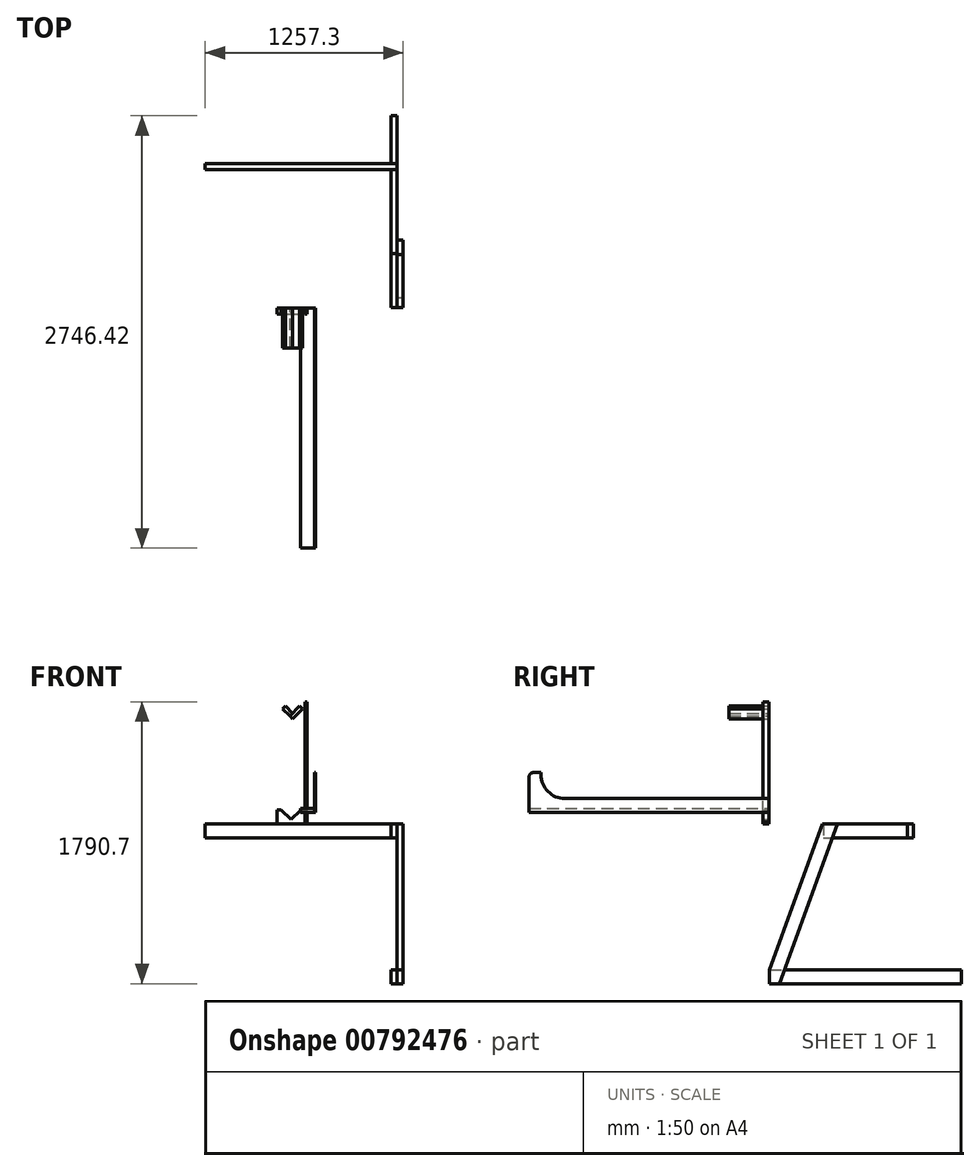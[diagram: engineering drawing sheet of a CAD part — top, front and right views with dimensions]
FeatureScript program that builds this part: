
annotation { "Feature Type Name" : "Feature", "Feature Type Description" : "" }
export const myFeature = defineFeature(function(context is Context, id is Id, definition is map)
    precondition{}
    {
        {
            var Q0;
            Q0=qCreatedBy(makeId("Right.planeOp"),FACE);
            var sketch = newSketch(context, id + "F0", { "sketchPlane" : qUnion([Q0])});
            skCircle(sketch, "E0", {"center": v(0, 368.3) * mm, "radius": 368.3 * mm, "construction": true});
            skLineSegment(sketch, "E1", {"start": v(0, 0) * mm, "end": v(2298.17, 0) * mm, "construction": true});
            skLineSegment(sketch, "E2", {"start": v(-368.3, 745.94) * mm, "end": v(-368.3, 0) * mm, "construction": true});
            skCircle(sketch, "E3", {"center": v(1157.3, 368.3) * mm, "radius": 368.3 * mm, "construction": true});
            skLineSegment(sketch, "E4", {"start": v(281.32, 941.93) * mm, "end": v(431.44, 558.5) * mm, "construction": true});
            skLineSegment(sketch, "E5", {"start": v(348.24, 558.5) * mm, "end": v(0, 368.3) * mm, "construction": true});
            skLineSegment(sketch, "E6", {"start": v(0, 368.3) * mm, "end": v(431.44, 343.27) * mm, "construction": true});
            skLineSegment(sketch, "E7", {"start": v(431.44, 343.27) * mm, "end": v(567.09, 368.3) * mm, "construction": true});
            skLineSegment(sketch, "E8", {"start": v(567.09, 368.3) * mm, "end": v(811.25, 847.88) * mm, "construction": true});
            skLineSegment(sketch, "E9", {"start": v(811.25, 847.88) * mm, "end": v(912.54, 907.57) * mm, "construction": true});
            skLineSegment(sketch, "E10", {"start": v(867.32, 967.25) * mm, "end": v(1120.53, 368.3) * mm, "construction": true});
            skLineSegment(sketch, "E11", {"start": v(867.32, 967.25) * mm, "end": v(409.73, 650.74) * mm, "construction": true});
            skLineSegment(sketch, "E12", {"start": v(346.7, 774.93) * mm, "end": v(556.87, 752.52) * mm, "construction": true});
            skLineSegment(sketch, "E13", {"start": v(125.78, 1032.36) * mm, "end": v(384.41, 1032.36) * mm, "construction": true});
            skCircle(sketch, "E14", {"center": v(1157.3, 368.3) * mm, "radius": 101.6 * mm, "construction": true});
            skCircle(sketch, "E15", {"center": v(0, 368.3) * mm, "radius": 88.9 * mm, "construction": true});
            skSolve(sketch);
        }
        {
            var Q0;
            Q0=qCreatedBy(makeId("Right.planeOp"),FACE);
            var sketch = newSketch(context, id + "F1", { "sketchPlane" : qUnion([Q0])});
            skCircle(sketch, "E16", {"center": v(0, 1519.87) * mm, "radius": 368.3 * mm});
            skCircle(sketch, "E17", {"center": v(1155.64, 1531.5) * mm, "radius": 368.3 * mm});
            skLineSegment(sketch, "E18", {"start": v(0, 1519.87) * mm, "end": v(1155.64, 1531.5) * mm});
            skLineSegment(sketch, "E19", {"start": v(120.35, 2245.02) * mm, "end": v(884.9, 2252.7) * mm});
            skLineSegment(sketch, "E20", {"start": v(0, 1519.87) * mm, "end": v(120.35, 2245.02) * mm});
            skLineSegment(sketch, "E21", {"start": v(884.9, 2252.7) * mm, "end": v(1155.64, 1531.5) * mm});
            skSolve(sketch);
        }
        {
            var Q0;
            Q0=qCreatedBy(makeId("Right.planeOp"),FACE);
            var sketch = newSketch(context, id + "F2", { "sketchPlane" : qUnion([Q0])});
            skLineSegment(sketch, "E22.bottom", {"start": v(3.22, 177.8) * mm, "end": v(1222.42, 177.8) * mm});
            skLineSegment(sketch, "E22.top", {"start": v(3.22, 88.9) * mm, "end": v(1222.42, 88.9) * mm});
            skLineSegment(sketch, "E22.left", {"start": v(3.22, 177.8) * mm, "end": v(3.22, 88.9) * mm});
            skLineSegment(sketch, "E22.right", {"start": v(1222.42, 177.8) * mm, "end": v(1222.42, 88.9) * mm});
            skLineSegment(sketch, "E23.bottom", {"start": v(308.02, 1104.9) * mm, "end": v(917.62, 1104.9) * mm});
            skLineSegment(sketch, "E23.top", {"start": v(308.02, 1016) * mm, "end": v(917.62, 1016) * mm});
            skLineSegment(sketch, "E23.left", {"start": v(308.02, 1104.9) * mm, "end": v(308.02, 1016) * mm});
            skLineSegment(sketch, "E23.right", {"start": v(917.62, 1104.9) * mm, "end": v(917.62, 1016) * mm});
            skLineSegment(sketch, "E24", {"start": v(308.02, 1016) * mm, "end": v(3.22, 177.8) * mm});
            skLineSegment(sketch, "E25", {"start": v(917.62, 1016) * mm, "end": v(1222.42, 177.8) * mm});
            skLineSegment(sketch, "E26", {"start": v(823.02, 1016) * mm, "end": v(1127.82, 177.8) * mm});
            skLineSegment(sketch, "E27", {"start": v(434.94, 1104.9) * mm, "end": v(65.49, 88.9) * mm});
            skPoint(sketch, "E28", {"position": v(612.82, 1016) * mm});
            skPoint(sketch, "E29", {"position": v(612.82, 177.8) * mm});
            skPoint(sketch, "E30", {"position": v(612.82, 1104.9) * mm});
            skLineSegment(sketch, "E31", {"start": v(879.52, 1104.9) * mm, "end": v(879.52, 1016) * mm});
            skLineSegment(sketch, "E32", {"start": v(346.12, 1104.9) * mm, "end": v(346.12, 1016) * mm});
            skLineSegment(sketch, "E33", {"start": v(3.22, 177.8) * mm, "end": v(308.02, 1104.9) * mm, "construction": true});
            skSolve(sketch);
        }
        {
            var Q0;
            Q0=qCreatedBy(makeId("Right.planeOp"),FACE);
            var sketch = newSketch(context, id + "F3", { "sketchPlane" : qUnion([Q0])});
            skLineSegment(sketch, "E34.bottom", {"start": v(346.12, 1104.9) * mm, "end": v(879.52, 1104.9) * mm});
            skLineSegment(sketch, "E34.top", {"start": v(346.12, 1016) * mm, "end": v(879.52, 1016) * mm});
            skLineSegment(sketch, "E34.left", {"start": v(346.12, 1104.9) * mm, "end": v(346.12, 1016) * mm});
            skLineSegment(sketch, "E34.right", {"start": v(879.52, 1104.9) * mm, "end": v(879.52, 1016) * mm});
            skSolve(sketch);
        }
        {
            var Q0;
            Q0 = qSketchRegion(id + "F3", true);
            extrude(context, id + "F4", {"entities" : qUnion([Q0]), "oppositeDirection" : true, "depth" : 38.1 * mm, "offsetDistance" : 25.4 * mm});
        }
        {
            var Q0;
            Q0=qCreatedBy(makeId("Right.planeOp"),FACE);
            var sketch = newSketch(context, id + "F5", { "sketchPlane" : qUnion([Q0])});
            skLineSegment(sketch, "E35.bottom", {"start": v(879.52, 1104.9) * mm, "end": v(917.62, 1104.9) * mm});
            skLineSegment(sketch, "E35.top", {"start": v(879.52, 1016) * mm, "end": v(917.62, 1016) * mm});
            skLineSegment(sketch, "E35.left", {"start": v(879.52, 1104.9) * mm, "end": v(879.52, 1016) * mm});
            skLineSegment(sketch, "E35.right", {"start": v(917.62, 1104.9) * mm, "end": v(917.62, 1016) * mm});
            skSolve(sketch);
        }
        {
            var Q0;
            Q0 = qSketchRegion(id + "F5", true);
            extrude(context, id + "F6", {"entities" : qUnion([Q0]), "oppositeDirection" : true, "depth" : 1219.2 * mm, "offsetDistance" : 25.4 * mm});
        }
        {
            var Q0;
            Q0=qCreatedBy(makeId("Right.planeOp"),FACE);
            var sketch = newSketch(context, id + "F7", { "sketchPlane" : qUnion([Q0])});
            skLineSegment(sketch, "E36", {"start": v(434.94, 1104.9) * mm, "end": v(65.49, 88.9) * mm});
            skLineSegment(sketch, "E37", {"start": v(65.49, 88.9) * mm, "end": v(3.22, 88.9) * mm});
            skLineSegment(sketch, "E38", {"start": v(340.35, 1104.9) * mm, "end": v(3.22, 177.8) * mm});
            skLineSegment(sketch, "E39", {"start": v(434.94, 1104.9) * mm, "end": v(340.35, 1104.9) * mm});
            skLineSegment(sketch, "E40", {"start": v(3.22, 88.9) * mm, "end": v(3.22, 177.8) * mm});
            skSolve(sketch);
        }
        {
            var Q0;
            Q0 = qSketchRegion(id + "F7", true);
            extrude(context, id + "F8", {"entities" : qUnion([Q0]), "depth" : 38.1 * mm, "offsetDistance" : 25.4 * mm});
        }
        {
            var Q0;
            Q0=qCreatedBy(makeId("Right.planeOp"),FACE);
            var sketch = newSketch(context, id + "F9", { "sketchPlane" : qUnion([Q0])});
            skLineSegment(sketch, "E41.bottom", {"start": v(3.22, 177.8) * mm, "end": v(1222.42, 177.8) * mm});
            skLineSegment(sketch, "E41.top", {"start": v(3.22, 88.9) * mm, "end": v(1222.42, 88.9) * mm});
            skLineSegment(sketch, "E41.left", {"start": v(3.22, 177.8) * mm, "end": v(3.22, 88.9) * mm});
            skLineSegment(sketch, "E41.right", {"start": v(1222.42, 177.8) * mm, "end": v(1222.42, 88.9) * mm});
            skSolve(sketch);
        }
        {
            var Q0;
            Q0 = qSketchRegion(id + "F9", true);
            extrude(context, id + "F10", {"entities" : qUnion([Q0]), "oppositeDirection" : true, "depth" : 38.1 * mm, "offsetDistance" : 25.4 * mm});
        }
        {
            var Q0;
            Q0=qCreatedBy(makeId("Front.planeOp"),FACE);
            var sketch = newSketch(context, id + "F11", { "sketchPlane" : qUnion([Q0])});
            skLineSegment(sketch, "E42.bottom", {"start": v(-525.22, 1200.74) * mm, "end": v(-614.12, 1200.74) * mm});
            skLineSegment(sketch, "E42.top", {"start": v(-525.22, 1175.34) * mm, "end": v(-614.12, 1175.34) * mm});
            skLineSegment(sketch, "E42.left", {"start": v(-525.22, 1200.74) * mm, "end": v(-525.22, 1175.34) * mm});
            skLineSegment(sketch, "E42.right", {"start": v(-614.12, 1200.74) * mm, "end": v(-614.12, 1175.34) * mm});
            skSolve(sketch);
        }
        {
            var Q0;
            Q0 = qSketchRegion(id + "F11", true);
            extrude(context, id + "F12", {"entities" : qUnion([Q0]), "depth" : 1524 * mm, "offsetDistance" : 25.4 * mm});
        }
        {
            var Q0;
            Q0=qCreatedBy(makeId("Front.planeOp"),FACE);
            var sketch = newSketch(context, id + "F13", { "sketchPlane" : qUnion([Q0])});
            skLineSegment(sketch, "E43.bottom", {"start": v(-525.22, 1175.34) * mm, "end": v(-518.87, 1175.34) * mm});
            skLineSegment(sketch, "E43.top", {"start": v(-525.22, 1429.34) * mm, "end": v(-518.87, 1429.34) * mm});
            skLineSegment(sketch, "E43.left", {"start": v(-525.22, 1175.34) * mm, "end": v(-525.22, 1429.34) * mm});
            skLineSegment(sketch, "E43.right", {"start": v(-518.87, 1175.34) * mm, "end": v(-518.87, 1429.34) * mm});
            skSolve(sketch);
        }
        {
            var Q0;
            Q0 = qSketchRegion(id + "F13", true);
            extrude(context, id + "F14", {"entities" : qUnion([Q0]), "depth" : 1524 * mm, "offsetDistance" : 25.4 * mm});
        }
        {
            var Q0;
            Q0=makeQuery(id+"F14.opExtrude","SWEPT_FACE",FACE,{"disambiguationData":[OSD([sQuery(id+"F13.wireOp",EDGE,"E43.left")])]});
            var sketch = newSketch(context, id + "F15", { "sketchPlane" : qUnion([Q0])});
            skLineSegment(sketch, "E44.bottom", {"start": v(0, 1429.34) * mm, "end": v(1447.8, 1429.34) * mm});
            skLineSegment(sketch, "E44.top", {"start": v(0, 1264.24) * mm, "end": v(1295.4, 1264.24) * mm});
            skLineSegment(sketch, "E44.left", {"start": v(0, 1429.34) * mm, "end": v(0, 1264.24) * mm});
            skLineSegment(sketch, "E44.right", {"start": v(1447.8, 1429.34) * mm, "end": v(1447.8, 1416.64) * mm});
            skPoint(sketch, "E45.visualSharp", {"position": v(1447.8, 1264.24) * mm});
            skArc(sketch, "E45.filletArc", {"start": v(1295.4, 1264.24) * mm, "mid": v(1403.16, 1308.88) * mm, "end": v(1447.8, 1416.64) * mm});
            skSolve(sketch);
        }
        {
            var Q0;
            Q0 = qSketchRegion(id + "F15", true);
            extrude(context, id + "F16", {"entities" : qUnion([Q0]), "operationType" : NewBodyOperationType.REMOVE, "oppositeDirection" : true, "depth" : 25.4 * mm, "offsetDistance" : 25.4 * mm});
        }
        {
            var Q0;
            Q0=makeQuery(id+"F16.boolean.opBoolean","COPY",EDGE,{"derivedFrom":makeQuery(id+"F16.opExtrude","SWEPT_EDGE",EDGE,{"disambiguationData":[OSD([sQuery(id+"F13.wireOp",EDGE,"E43.left"),sQuery(id+"F15.wireOp",EDGE,"E44.top"),sQuery(id+"F15.wireOp",EDGE,"E44.left")])]})});
            var Q1;
            Q1=makeQuery(id+"F16.boolean.opBoolean","COPY",EDGE,{"derivedFrom":makeQuery(id+"F16.opExtrude","SWEPT_EDGE",EDGE,{"disambiguationData":[OSD([sQuery(id+"F13.wireOp",EDGE,"E43.top"),sQuery(id+"F13.wireOp",EDGE,"E43.left"),sQuery(id+"F15.wireOp",EDGE,"E44.bottom"),sQuery(id+"F15.wireOp",EDGE,"E44.right")])]})});
            var Q2;
            Q2=makeQuery(id+"F14.opExtrude","CAP_EDGE",EDGE,{"disambiguationData":[OSD([sQuery(id+"F13.wireOp",EDGE,"E43.top")])],"isStart":false});
            fillet(context, id + "F17", {"entities" : qUnion([Q0, Q1, Q2]), "radius" : 25.4 * mm, "tangentPropagation" : true, "allowEdgeOverflow" : false});
        }
        {
            var Q0;
            Q0=qCreatedBy(makeId("Front.planeOp"),FACE);
            var sketch = newSketch(context, id + "F18", { "sketchPlane" : qUnion([Q0])});
            skLineSegment(sketch, "E46", {"start": v(-673.76, 1130.94) * mm, "end": v(-736.62, 1193.8) * mm});
            skLineSegment(sketch, "E47", {"start": v(-673.76, 1130.94) * mm, "end": v(-610.9, 1193.8) * mm});
            skLineSegment(sketch, "E48.0", {"start": v(-762.45, 1078.17) * mm, "end": v(-699.59, 1141.03) * mm});
            skLineSegment(sketch, "E49.0", {"start": v(-673.76, 1166.86) * mm, "end": v(-718.66, 1211.76) * mm});
            skLineSegment(sketch, "E50", {"start": v(-736.62, 1193.8) * mm, "end": v(-718.66, 1211.76) * mm});
            skLineSegment(sketch, "E51", {"start": v(-699.59, 1141.03) * mm, "end": v(-610.9, 1193.8) * mm});
            skCircle(sketch, "E52", {"center": v(-673.76, 1220.74) * mm, "radius": 38.1 * mm, "construction": true});
            skLineSegment(sketch, "E53", {"start": v(-673.76, 1166.86) * mm, "end": v(-673.76, 1220.74) * mm, "construction": true});
            skLineSegment(sketch, "E54.top", {"start": v(-762.02, 1104.9) * mm, "end": v(-585.5, 1104.9) * mm});
            skLineSegment(sketch, "E54.left", {"start": v(-762.02, 1193.8) * mm, "end": v(-762.02, 1104.9) * mm});
            skLineSegment(sketch, "E54.right", {"start": v(-585.5, 1193.8) * mm, "end": v(-585.5, 1104.9) * mm});
            skLineSegment(sketch, "E55", {"start": v(-610.9, 1193.8) * mm, "end": v(-585.5, 1193.8) * mm});
            skLineSegment(sketch, "E56", {"start": v(-736.62, 1193.8) * mm, "end": v(-762.02, 1193.8) * mm});
            skCircle(sketch, "E57", {"center": v(-673.76, 1881.14) * mm, "radius": 38.1 * mm, "construction": true});
            skLineSegment(sketch, "E58", {"start": v(-948.86, 1550.94) * mm, "end": v(-526.99, 1550.94) * mm, "construction": true});
            skArc(sketch, "E59", {"start": v(-635.86, 1681.85) * mm, "mid": v(-673.76, 1716.04) * mm, "end": v(-711.66, 1681.85) * mm, "construction": true});
            skLineSegment(sketch, "E60", {"start": v(-585.5, 1193.8) * mm, "end": v(-635.86, 1681.85) * mm, "construction": true});
            skPoint(sketch, "E61.orphan", {"position": v(-762.02, 756.82) * mm});
            skPoint(sketch, "E62.orphan", {"position": v(-585.5, 2599.06) * mm});
            skLineSegment(sketch, "E63", {"start": v(-762.02, 1193.8) * mm, "end": v(-711.66, 1681.85) * mm, "construction": true});
            skSolve(sketch);
        }
        {
            var Q0;
            Q0=qCreatedBy(makeId("Front.planeOp"),FACE);
            var sketch = newSketch(context, id + "F19", { "sketchPlane" : qUnion([Q0])});
            skLineSegment(sketch, "E64", {"start": v(-726.38, 1833.77) * mm, "end": v(-681.48, 1788.87) * mm});
            skLineSegment(sketch, "E65", {"start": v(-681.48, 1788.87) * mm, "end": v(-663.52, 1806.83) * mm});
            skLineSegment(sketch, "E66", {"start": v(-663.52, 1806.83) * mm, "end": v(-708.42, 1851.73) * mm});
            skLineSegment(sketch, "E67", {"start": v(-708.42, 1851.73) * mm, "end": v(-726.38, 1833.77) * mm});
            skSolve(sketch);
        }
        {
            var Q0;
            Q0 = qSketchRegion(id + "F19", true);
            extrude(context, id + "F20", {"entities" : qUnion([Q0]), "depth" : 254 * mm, "offsetDistance" : 25.4 * mm});
        }
        {
            var Q0;
            Q0=qCreatedBy(makeId("Front.planeOp"),FACE);
            var sketch = newSketch(context, id + "F21", { "sketchPlane" : qUnion([Q0])});
            skLineSegment(sketch, "E68", {"start": v(-663.52, 1770.9) * mm, "end": v(-600.65, 1833.77) * mm});
            skLineSegment(sketch, "E69", {"start": v(-600.65, 1833.77) * mm, "end": v(-618.61, 1851.73) * mm});
            skLineSegment(sketch, "E70", {"start": v(-618.61, 1851.73) * mm, "end": v(-681.48, 1788.87) * mm});
            skLineSegment(sketch, "E71", {"start": v(-681.48, 1788.87) * mm, "end": v(-663.52, 1770.9) * mm});
            skSolve(sketch);
        }
        {
            var Q0;
            Q0 = qSketchRegion(id + "F21", true);
            extrude(context, id + "F22", {"entities" : qUnion([Q0]), "depth" : 254 * mm, "offsetDistance" : 25.4 * mm});
        }
        {
            var Q0;
            {var subQ0=sQuery(id+"F18.wireOp",EDGE,"E47");Q0=makeQuery(id+"F18.imprint","IMPRINT",FACE,{"disambiguationData":[TD([[makeQuery(id+"F18.imprint","IMPRINT",EDGE,{"derivedFrom":subQ0}),-1.0]])]});}
            var sketch = newSketch(context, id + "F23", { "sketchPlane" : qUnion([Q0])});
            skLineSegment(sketch, "E72.bottom", {"start": v(-762.02, 1193.8) * mm, "end": v(-736.62, 1193.8) * mm});
            skLineSegment(sketch, "E72.top", {"start": v(-762.02, 1104.9) * mm, "end": v(-585.5, 1104.9) * mm});
            skLineSegment(sketch, "E72.left", {"start": v(-762.02, 1193.8) * mm, "end": v(-762.02, 1104.9) * mm});
            skLineSegment(sketch, "E72.right", {"start": v(-585.5, 1193.8) * mm, "end": v(-585.5, 1104.9) * mm});
            skLineSegment(sketch, "E73", {"start": v(-736.62, 1193.8) * mm, "end": v(-673.76, 1130.94) * mm});
            skLineSegment(sketch, "E74", {"start": v(-673.76, 1130.94) * mm, "end": v(-610.9, 1193.8) * mm});
            skLineSegment(sketch, "E75.trimOffspring", {"start": v(-610.9, 1193.8) * mm, "end": v(-585.5, 1193.8) * mm});
            skSolve(sketch);
        }
        {
            var Q0;
            Q0 = qSketchRegion(id + "F23", true);
            extrude(context, id + "F24", {"entities" : qUnion([Q0]), "depth" : 38.1 * mm, "offsetDistance" : 25.4 * mm});
        }
        {
            var Q0;
            {var subQ0=sQuery(id+"F18.wireOp",EDGE,"E47");Q0=makeQuery(id+"F18.imprint","IMPRINT",FACE,{"disambiguationData":[TD([[makeQuery(id+"F18.imprint","IMPRINT",EDGE,{"derivedFrom":subQ0}),-1.0]])]});}
            var sketch = newSketch(context, id + "F25", { "sketchPlane" : qUnion([Q0])});
            skLineSegment(sketch, "E76.bottom", {"start": v(-585.5, 1117.6) * mm, "end": v(-572.8, 1117.6) * mm});
            skLineSegment(sketch, "E76.top", {"start": v(-585.5, 1879.6) * mm, "end": v(-572.8, 1879.6) * mm});
            skLineSegment(sketch, "E76.left", {"start": v(-585.5, 1117.6) * mm, "end": v(-585.5, 1879.6) * mm});
            skLineSegment(sketch, "E76.right", {"start": v(-572.8, 1117.6) * mm, "end": v(-572.8, 1879.6) * mm});
            skCircle(sketch, "E77", {"center": v(-673.76, 1881.14) * mm, "radius": 38.1 * mm, "construction": true});
            skSolve(sketch);
        }
        {
            var Q0;
            Q0 = qSketchRegion(id + "F25", true);
            extrude(context, id + "F26", {"entities" : qUnion([Q0]), "depth" : 38.1 * mm, "offsetDistance" : 25.4 * mm});
        }
        {
            var Q0;
            Q0=makeQuery(id+"F24.opExtrude","CAP_VERTEX",VERTEX,{"disambiguationData":[OSD([sQuery(id+"F23.wireOp",EDGE,"E73"),sQuery(id+"F23.wireOp",EDGE,"E74")])],"isStart":false});
            var Q1;
            Q1=makeQuery(id+"F24.opExtrude","CAP_EDGE",EDGE,{"disambiguationData":[OSD([sQuery(id+"F23.wireOp",EDGE,"E72.top")])],"isStart":false});
            cPlane(context, id + "F27", {"entities" : qUnion([Q0, Q1]), "cplaneType" : CPlaneType.LINE_POINT, "offset" : 25.4 * mm, "width" : 152.4 * mm, "height" : 152.4 * mm});
        }
    });
